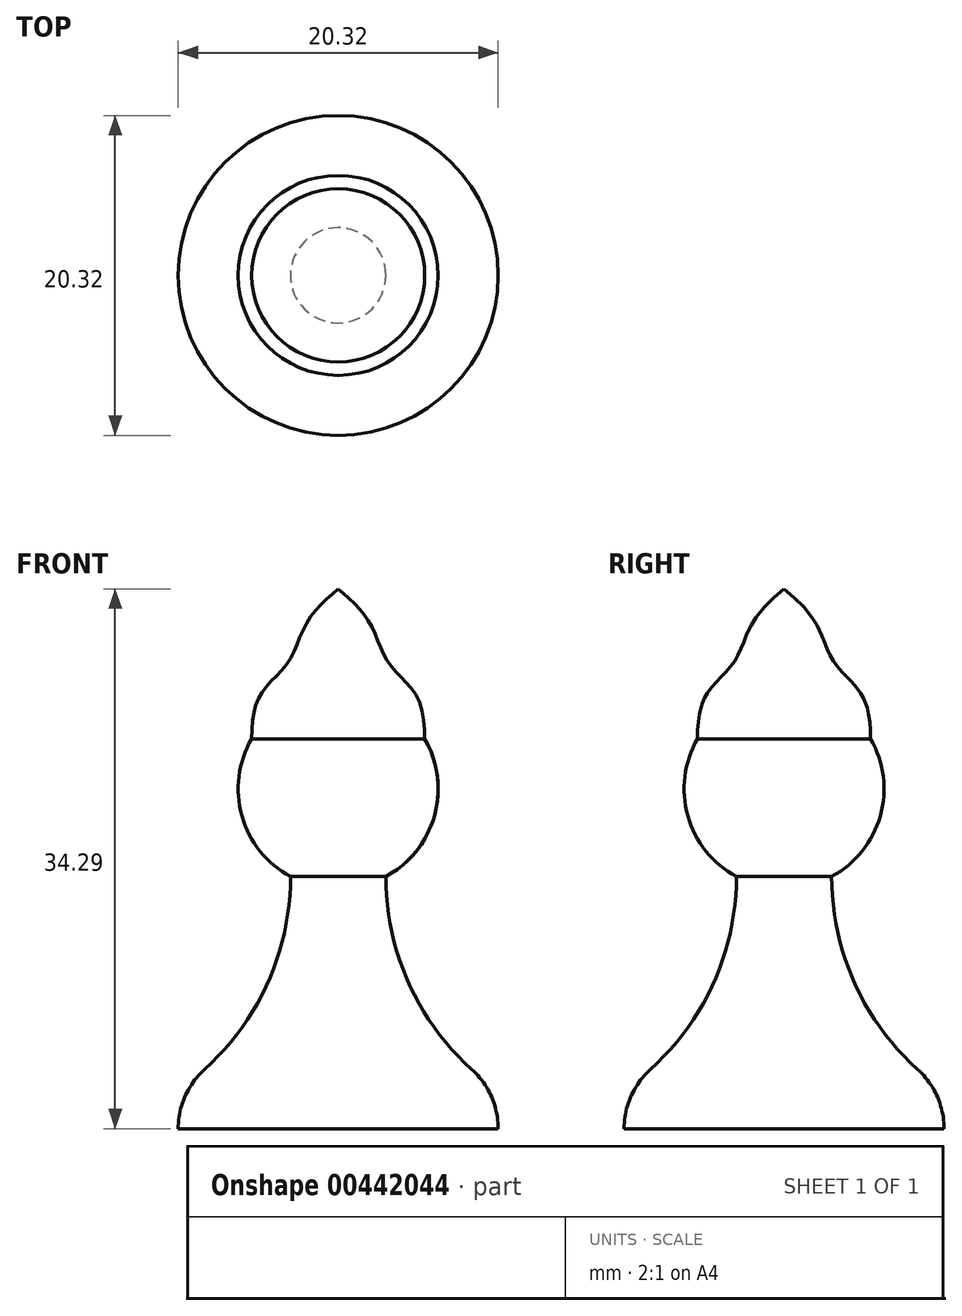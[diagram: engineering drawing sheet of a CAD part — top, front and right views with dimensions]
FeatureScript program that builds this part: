
annotation { "Feature Type Name" : "Feature", "Feature Type Description" : "" }
export const myFeature = defineFeature(function(context is Context, id is Id, definition is map)
    precondition{}
    {
        {
            var Q0;
            Q0=qCreatedBy(makeId("Front.planeOp"),FACE);
            var sketch = newSketch(context, id + "F0", { "sketchPlane" : qUnion([Q0])});
            skArc(sketch, "E0", {"start": v(0, 27.94) * mm, "mid": v(-6.35, 21.6) * mm, "end": v(0, 15.24) * mm});
            skLineSegment(sketch, "E1", {"start": v(0, 0) * mm, "end": v(-10.16, 0) * mm});
            skArc(sketch, "E2", {"start": v(-8.48, 3.77) * mm, "mid": v(-9.72, 2.07) * mm, "end": v(-10.16, 0) * mm});
            skArc(sketch, "E3", {"start": v(-8.48, 3.77) * mm, "mid": v(-4.45, 9.31) * mm, "end": v(-3.02, 16) * mm});
            skLineSegment(sketch, "E4", {"start": v(-3.02, 16) * mm, "end": v(-3.02, 0) * mm, "construction": true});
            skLineSegment(sketch, "E5", {"start": v(0, 27.94) * mm, "end": v(0, 0) * mm});
            skLineSegment(sketch, "E6", {"start": v(-10.16, 0) * mm, "end": v(-10.16, 3.2) * mm, "construction": true});
            skPoint(sketch, "E7", {"position": v(0, 24.77) * mm});
            skLineSegment(sketch, "E8", {"start": v(0, 24.77) * mm, "end": v(-5.5, 24.77) * mm});
            skLineSegment(sketch, "E9", {"start": v(0, 34.3) * mm, "end": v(0, 27.94) * mm});
            skFitSpline(sketch, "E10", {"points": [v(-5.5, 24.77) * mm, v(-4.86, 27.69) * mm, v(-3.17, 29.64) * mm, v(-1.97, 32.17) * mm, v(0, 34.3) * mm], "startDerivative": vector(0.01, 14.3) * mm, "endDerivative": vector(8.33, 7.05) * mm});
            skSolve(sketch);
        }
        {
            var Q0;
            Q0=qSketchRegion(id+"F0",true);
            var Q1;
            Q1=sQuery(id+"F0.wireOp",EDGE,"E5");
            revolve(context, id + "F1", {"entities" : qUnion([Q0]), "axis" : qUnion([Q1]), "revolveType" : RevolveType.FULL});
        }
    });
